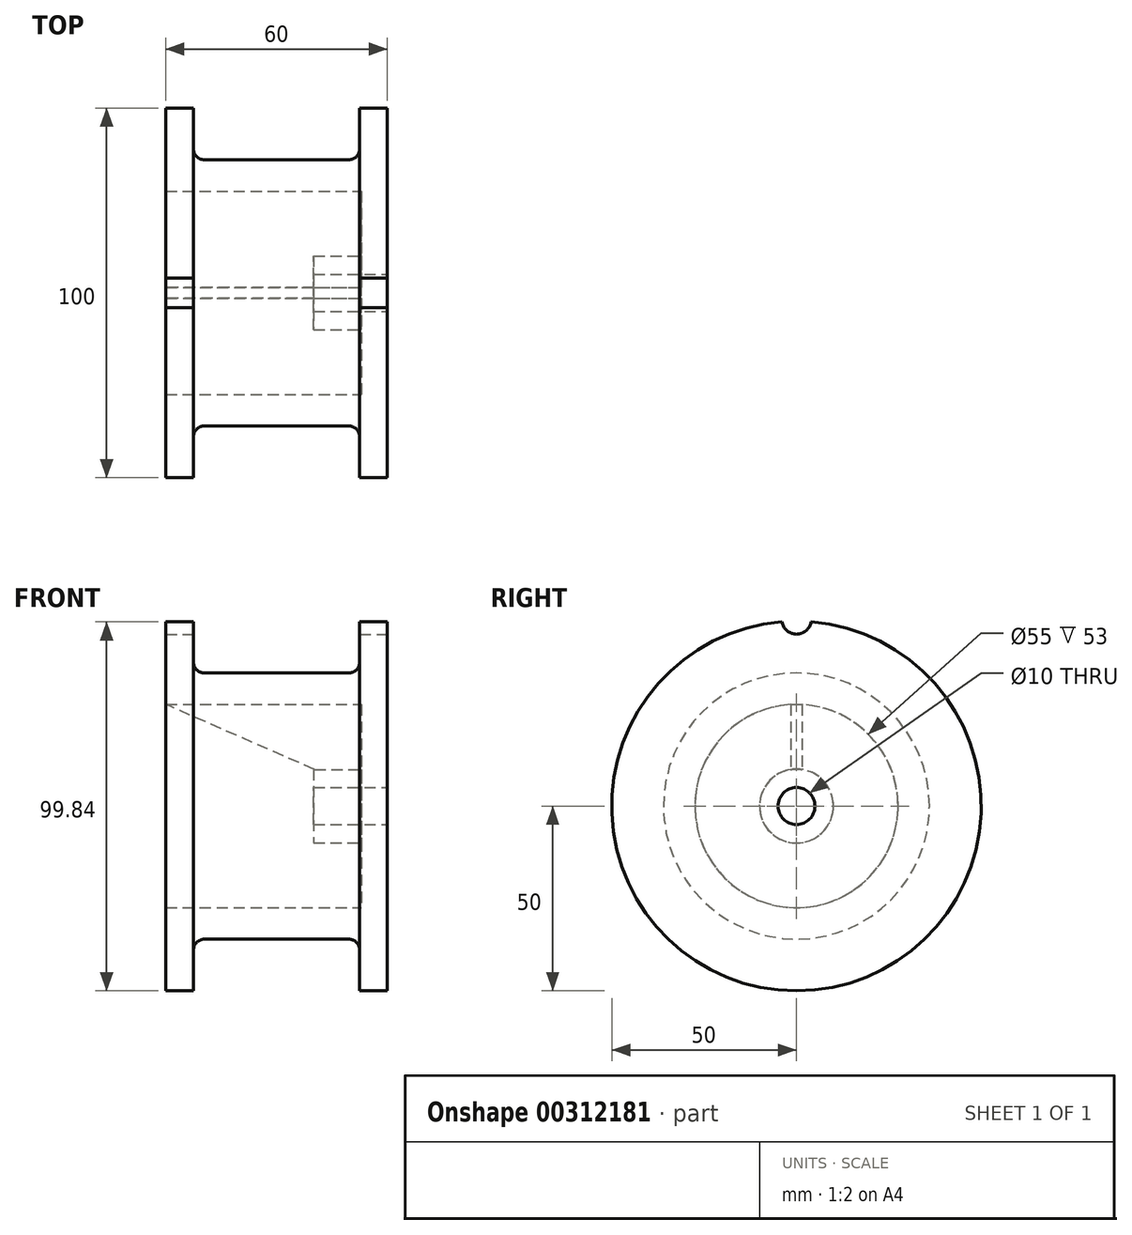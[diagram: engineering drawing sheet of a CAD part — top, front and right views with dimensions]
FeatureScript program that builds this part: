
annotation { "Feature Type Name" : "Feature", "Feature Type Description" : "" }
export const myFeature = defineFeature(function(context is Context, id is Id, definition is map)
    precondition{}
    {
        {
            var Q0;
            Q0=qCreatedBy(makeId("Right.planeOp"),FACE);
            var sketch = newSketch(context, id + "F0", { "sketchPlane" : qUnion([Q0])});
            skCircle(sketch, "E0", {"center": v(0, 0) * mm, "radius": 50 * mm});
            skSolve(sketch);
        }
        {
            var Q0;
            Q0=makeQuery(id+"F0.imprint","IMPRINT",FACE,{"disambiguationData":[TD([[makeQuery(id+"F0.imprint","IMPRINT",EDGE,{"derivedFrom":sQuery(id+"F0.wireOp",EDGE,"E0")}),1.0]])]});
            extrude(context, id + "F1", {"entities" : qUnion([Q0]), "endBound" : BoundingType.SYMMETRIC, "depth" : 60 * mm});
        }
        {
            var Q0;
            Q0=qCreatedBy(makeId("Front.planeOp"),FACE);
            var sketch = newSketch(context, id + "F2", { "sketchPlane" : qUnion([Q0])});
            skLineSegment(sketch, "E1.bottom", {"start": v(22.5, 50) * mm, "end": v(-22.5, 50) * mm});
            skLineSegment(sketch, "E1.top", {"start": v(22.5, 36) * mm, "end": v(-22.5, 36) * mm});
            skLineSegment(sketch, "E1.left", {"start": v(22.5, 50) * mm, "end": v(22.5, 36) * mm});
            skLineSegment(sketch, "E1.right", {"start": v(-22.5, 50) * mm, "end": v(-22.5, 36) * mm});
            skPoint(sketch, "E2", {"position": v(0, 36) * mm});
            skLineSegment(sketch, "E3.bottom", {"start": v(23, 0) * mm, "end": v(-30, 0) * mm});
            skLineSegment(sketch, "E3.top", {"start": v(23, 27.5) * mm, "end": v(-30, 27.5) * mm});
            skLineSegment(sketch, "E3.left", {"start": v(23, 10) * mm, "end": v(23, 27.5) * mm});
            skLineSegment(sketch, "E3.right", {"start": v(-30, 0) * mm, "end": v(-30, 27.5) * mm});
            skLineSegment(sketch, "E4", {"start": v(0, 0) * mm, "end": v(79.6, 0) * mm, "construction": true});
            skLineSegment(sketch, "E5", {"start": v(23, 5) * mm, "end": v(30, 5) * mm});
            skLineSegment(sketch, "E6", {"start": v(30, 5) * mm, "end": v(30, 0) * mm});
            skLineSegment(sketch, "E7", {"start": v(30, 0) * mm, "end": v(23, 0) * mm});
            skLineSegment(sketch, "E8", {"start": v(23, 5) * mm, "end": v(10, 5) * mm});
            skLineSegment(sketch, "E9", {"start": v(10, 5) * mm, "end": v(10, 10) * mm});
            skLineSegment(sketch, "E10", {"start": v(10, 10) * mm, "end": v(23, 10) * mm});
            skSolve(sketch);
        }
        {
            var Q0;
            Q0 = qSketchRegion(id + "F2", true);
            var Q1;
            Q1 = qConstructionFilter(qBodyType(qCreatedBy(id + "F2" ,EDGE), BodyType.WIRE), ConstructionObject.NO);
            var Q2;
            Q2=sQuery(id+"F2.wireOp",EDGE,"E4");
            revolve(context, id + "F3", {"operationType" : NewBodyOperationType.REMOVE, "entities" : qUnion([Q0]), "surfaceEntities" : qUnion([Q1]), "axis" : qUnion([Q2]), "revolveType" : RevolveType.FULL, "oppositeDirection" : true});
        }
        {
            var Q0;
            Q0=qCreatedBy(makeId("Right.planeOp"),FACE);
            var sketch = newSketch(context, id + "F4", { "sketchPlane" : qUnion([Q0])});
            skCircle(sketch, "E11", {"center": v(0, 50.5) * mm, "radius": 4 * mm});
            skSolve(sketch);
        }
        {
            var Q0;
            Q0=makeQuery(id+"F4.imprint","IMPRINT",FACE,{"disambiguationData":[TD([[makeQuery(id+"F4.imprint","IMPRINT",EDGE,{"derivedFrom":sQuery(id+"F4.wireOp",EDGE,"E11")}),1.0]])]});
            extrude(context, id + "F5", {"entities" : qUnion([Q0]), "operationType" : NewBodyOperationType.REMOVE, "endBound" : BoundingType.SYMMETRIC, "oppositeDirection" : true, "depth" : 60 * mm});
        }
        {
            var Q0;
            Q0=qCreatedBy(makeId("Front.planeOp"),FACE);
            var sketch = newSketch(context, id + "F6", { "sketchPlane" : qUnion([Q0])});
            skLineSegment(sketch, "E12", {"start": v(10.46, 9.8) * mm, "end": v(-30, 27.5) * mm});
            skLineSegment(sketch, "E13", {"start": v(-30, 27.5) * mm, "end": v(23, 27.5) * mm});
            skLineSegment(sketch, "E14", {"start": v(23, 27.5) * mm, "end": v(23, 9.8) * mm});
            skLineSegment(sketch, "E15", {"start": v(23, 9.8) * mm, "end": v(10.46, 9.8) * mm});
            skSolve(sketch);
        }
        {
            var Q0;
            Q0 = qSketchRegion(id + "F6", true);
            extrude(context, id + "F7", {"entities" : qUnion([Q0]), "operationType" : NewBodyOperationType.ADD, "endBound" : BoundingType.SYMMETRIC, "depth" : 3 * mm});
        }
        {
            var Q0;
            Q0=makeQuery(id+"F3.boolean.opBoolean","COPY",EDGE,{"derivedFrom":makeQuery(id+"F3.opRevolve","SWEPT_EDGE",EDGE,{"disambiguationData":[OSD([sQuery(id+"F2.wireOp",EDGE,"E1.top"),sQuery(id+"F2.wireOp",EDGE,"E1.left")])]})});
            var Q1;
            Q1=makeQuery(id+"F3.boolean.opBoolean","COPY",EDGE,{"derivedFrom":makeQuery(id+"F3.opRevolve","SWEPT_EDGE",EDGE,{"disambiguationData":[OSD([sQuery(id+"F2.wireOp",EDGE,"E1.top"),sQuery(id+"F2.wireOp",EDGE,"E1.right")])]})});
            fillet(context, id + "F8", {"entities" : qUnion([Q0, Q1]), "radius" : 3 * mm, "tangentPropagation" : true, "allowEdgeOverflow" : false});
        }
    });
